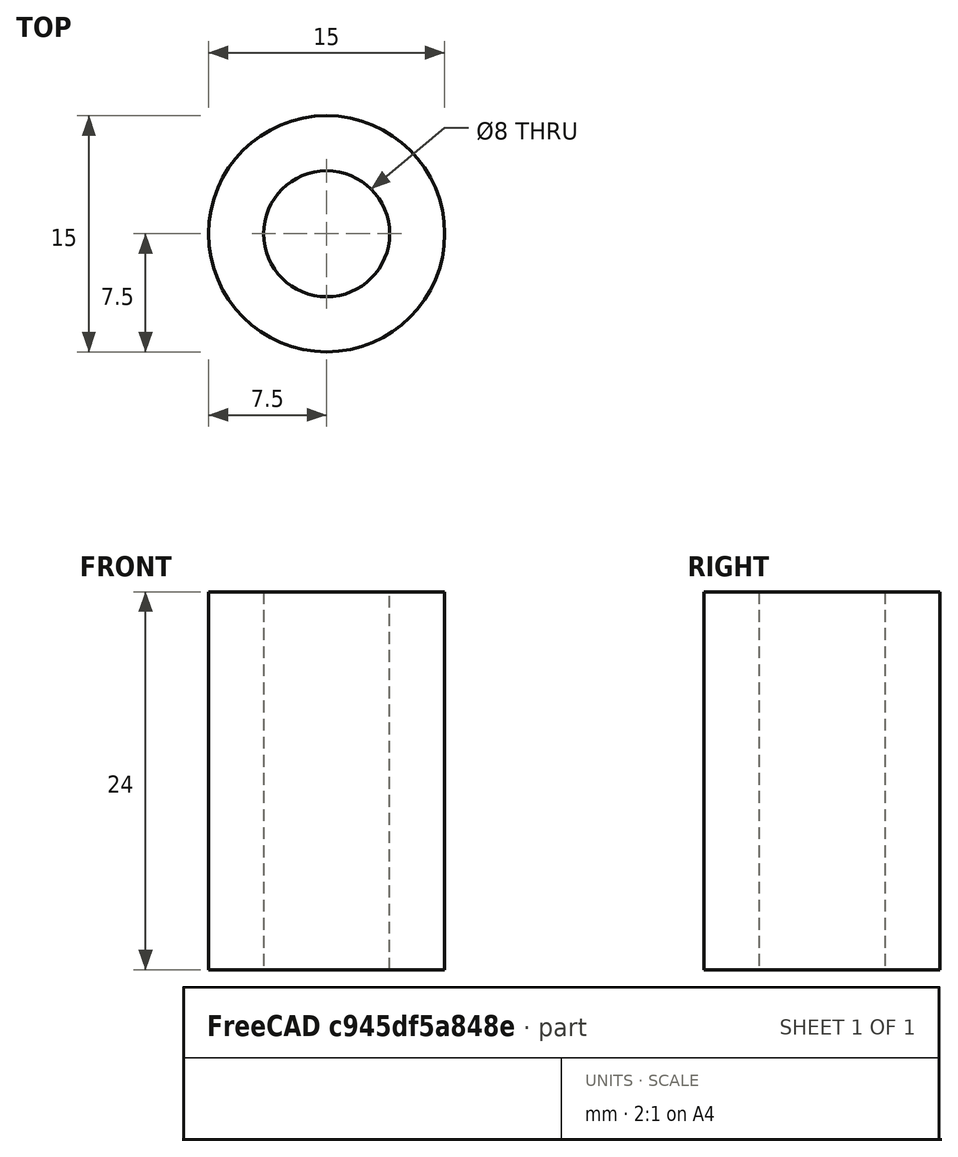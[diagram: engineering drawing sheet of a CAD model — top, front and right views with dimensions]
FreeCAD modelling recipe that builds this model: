
FCSTD DOCUMENT  (FreeCAD 0.18R14555 (Git shallow))
Label: round-bearing-short
License: All rights reserved
LicenseURL: http://en.wikipedia.org/wiki/All_rights_reserved
objects: Sketcher::SketchObject×1, PartDesign::Pad×1, PartDesign::Body×1
note: 4 computed .brp shape members not serialized (recipe doc carries the construction recipe); baked Part::Feature solids carry a one-line shape summary decoded from their .brp

FEATURE [Sketcher::SketchObject] Sketch
  MapMode = 5
  Support = -> [XY_Plane]
  sketch-geometry (2):
    g0: Circle CenterX=0 CenterY=0 CenterZ=0 NormalX=0 NormalY=0 NormalZ=1 AngleXU=0 Radius=4
    g1: Circle CenterX=0 CenterY=0 CenterZ=0 NormalX=0 NormalY=0 NormalZ=1 AngleXU=0 Radius=7.5
  constraints (4):
    c: Coincident(g0,g-1)
    c: Coincident(g1,g0)
    c: Radius(g0) = 4
    c: Radius(g1) = 7.5
FEATURE [PartDesign::Pad] Pad
  Length = 24
  Length2 = 100
  Profile = -> Sketch
  Type = 0
FEATURE [PartDesign::Body] Body
  Group = -> [Sketch,Pad]
  Origin = -> Origin
  Tip = -> Pad
